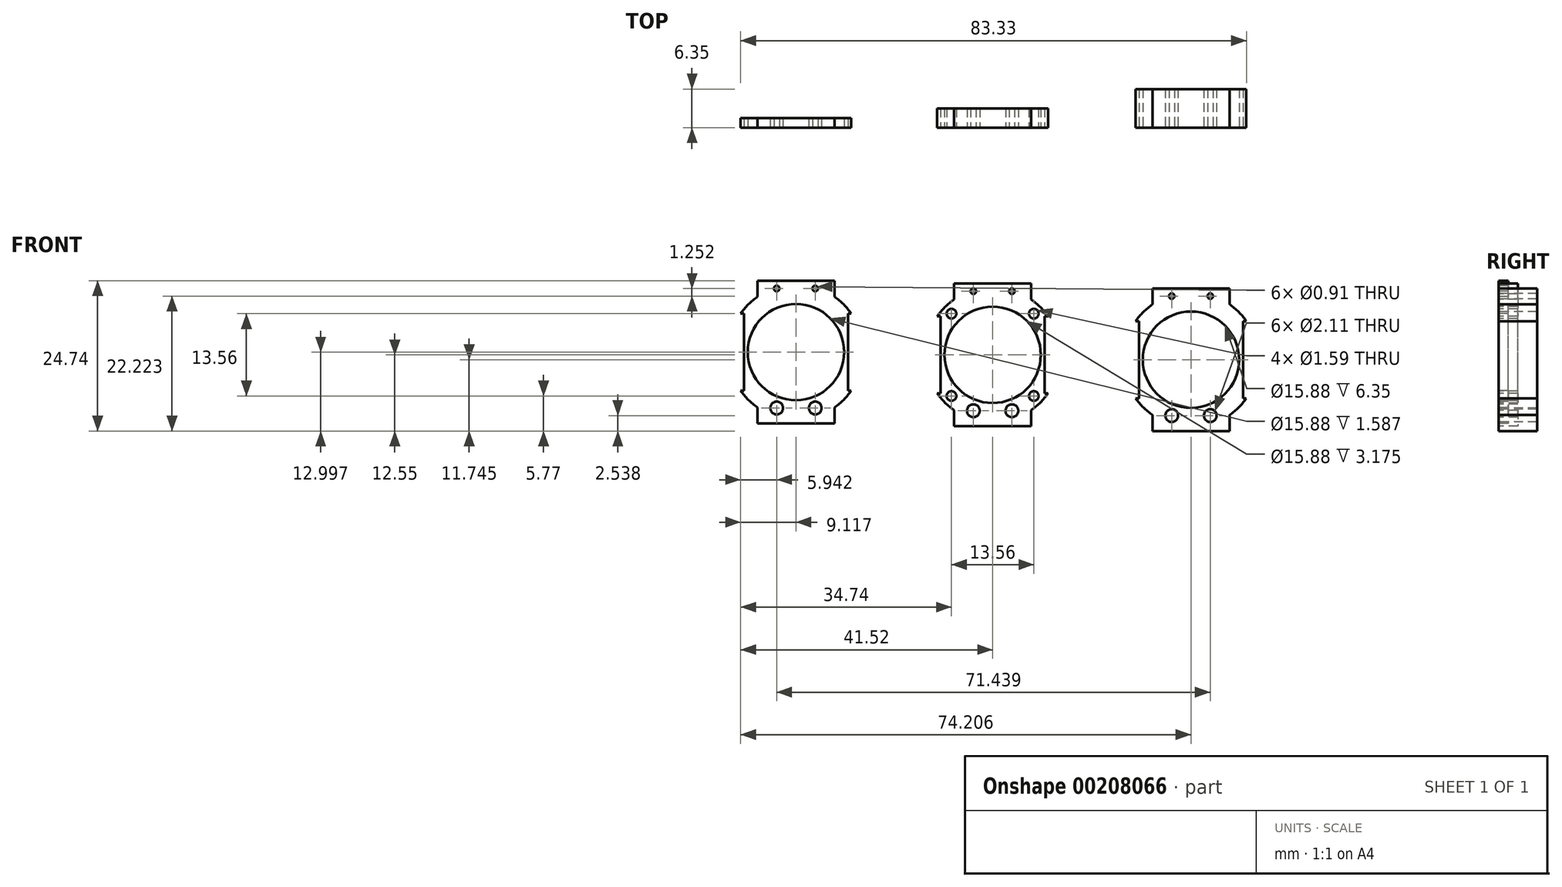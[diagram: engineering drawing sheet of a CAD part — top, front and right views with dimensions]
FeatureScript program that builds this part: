
annotation { "Feature Type Name" : "Feature", "Feature Type Description" : "" }
export const myFeature = defineFeature(function(context is Context, id is Id, definition is map)
    precondition{}
    {
        {
            var Q0;
            Q0=qCreatedBy(makeId("Front.planeOp"),FACE);
            var sketch = newSketch(context, id + "F0", { "sketchPlane" : qUnion([Q0])});
            skCircle(sketch, "E0", {"center": v(0, 0) * mm, "radius": 7.94 * mm});
            skCircle(sketch, "E1", {"center": v(0, 0) * mm, "radius": 11.11 * mm});
            skLineSegment(sketch, "E2", {"start": v(0, 15.5) * mm, "end": v(0, -17.4) * mm, "construction": true});
            skLineSegment(sketch, "E3", {"start": v(-15.84, 0) * mm, "end": v(17.27, 0) * mm, "construction": true});
            skLineSegment(sketch, "E4", {"start": v(-6.35, 12.66) * mm, "end": v(-6.35, -14.56) * mm, "construction": true});
            skLineSegment(sketch, "E5", {"start": v(6.35, -14.56) * mm, "end": v(6.35, 13.39) * mm, "construction": true});
            skLineSegment(sketch, "E6", {"start": v(-14.72, 6.35) * mm, "end": v(13.83, 6.35) * mm, "construction": true});
            skLineSegment(sketch, "E7", {"start": v(13.83, -6.35) * mm, "end": v(-15.12, -6.35) * mm, "construction": true});
            skLineSegment(sketch, "E8", {"start": v(0, 7.94) * mm, "end": v(-8.8, 7.94) * mm, "construction": true});
            skLineSegment(sketch, "E9", {"start": v(-7.94, 0) * mm, "end": v(-7.94, -9.09) * mm, "construction": true});
            skLineSegment(sketch, "E10", {"start": v(0, -7.94) * mm, "end": v(9.16, -7.94) * mm, "construction": true});
            skLineSegment(sketch, "E11", {"start": v(7.94, 0) * mm, "end": v(7.94, 8.95) * mm, "construction": true});
            skLineSegment(sketch, "E12", {"start": v(-6.35, 8.57) * mm, "end": v(6.35, 8.57) * mm});
            skLineSegment(sketch, "E13", {"start": v(6.35, 8.57) * mm, "end": v(6.35, 11.75) * mm});
            skLineSegment(sketch, "E14", {"start": v(6.35, 11.75) * mm, "end": v(-6.35, 11.75) * mm});
            skLineSegment(sketch, "E15", {"start": v(-6.35, 11.75) * mm, "end": v(-6.35, 8.57) * mm});
            skLineSegment(sketch, "E16", {"start": v(-8.57, -6.35) * mm, "end": v(-8.57, 6.35) * mm});
            skLineSegment(sketch, "E17", {"start": v(-8.57, 6.35) * mm, "end": v(-11.75, 6.35) * mm});
            skLineSegment(sketch, "E18", {"start": v(-11.75, 6.35) * mm, "end": v(-11.75, -6.35) * mm});
            skLineSegment(sketch, "E19", {"start": v(-11.75, -6.35) * mm, "end": v(-8.57, -6.35) * mm});
            skLineSegment(sketch, "E20", {"start": v(6.35, -8.57) * mm, "end": v(-6.35, -8.57) * mm});
            skLineSegment(sketch, "E21", {"start": v(-6.35, -8.57) * mm, "end": v(-6.35, -11.75) * mm});
            skLineSegment(sketch, "E22", {"start": v(-6.35, -11.75) * mm, "end": v(6.35, -11.75) * mm});
            skLineSegment(sketch, "E23", {"start": v(6.35, -11.75) * mm, "end": v(6.35, -8.57) * mm});
            skLineSegment(sketch, "E24", {"start": v(8.57, 6.35) * mm, "end": v(8.57, -6.35) * mm});
            skLineSegment(sketch, "E25", {"start": v(8.57, -6.35) * mm, "end": v(11.75, -6.35) * mm});
            skLineSegment(sketch, "E26", {"start": v(11.75, -6.35) * mm, "end": v(11.75, 6.35) * mm});
            skLineSegment(sketch, "E27", {"start": v(11.75, 6.35) * mm, "end": v(8.57, 6.35) * mm});
            skLineSegment(sketch, "E28", {"start": v(-7.33, 10.48) * mm, "end": v(7.08, 10.48) * mm, "construction": true});
            skPoint(sketch, "E29.startSnap0", {"position": v(-6.35, -10.16) * mm});
            skPoint(sketch, "E29.endSnap0", {"position": v(6.35, -10.16) * mm});
            skLineSegment(sketch, "E30", {"start": v(-3.17, 13.26) * mm, "end": v(-3.17, -13.35) * mm, "construction": true});
            skLineSegment(sketch, "E31", {"start": v(-3.17, -13.35) * mm, "end": v(3.18, -13.35) * mm, "construction": true});
            skLineSegment(sketch, "E32", {"start": v(3.18, -13.35) * mm, "end": v(3.18, 13.23) * mm, "construction": true});
            skCircle(sketch, "E33", {"center": v(-3.17, 10.48) * mm, "radius": 0.46 * mm});
            skCircle(sketch, "E34", {"center": v(3.18, 10.48) * mm, "radius": 0.46 * mm});
            skCircle(sketch, "E35", {"center": v(-3.17, -9.2) * mm, "radius": 1.05 * mm});
            skCircle(sketch, "E36", {"center": v(3.18, -9.2) * mm, "radius": 1.05 * mm});
            skLineSegment(sketch, "E37", {"start": v(-5.15, -9.2) * mm, "end": v(5.25, -9.2) * mm, "construction": true});
            skLineSegment(sketch, "E38", {"start": v(1.46, -9.2) * mm, "end": v(5.23, -9.2) * mm, "construction": true});
            skLineSegment(sketch, "E39", {"start": v(7.94, 0) * mm, "end": v(11.11, 0) * mm, "construction": true});
            skCircle(sketch, "E40", {"center": v(0, 0) * mm, "radius": 9.59 * mm, "construction": true});
            skLineSegment(sketch, "E41", {"start": v(0, 0) * mm, "end": v(-14.65, 14.65) * mm, "construction": true});
            skLineSegment(sketch, "E42", {"start": v(0, 0) * mm, "end": v(14.9, -14.9) * mm, "construction": true});
            skLineSegment(sketch, "E43", {"start": v(0, 0) * mm, "end": v(-14.95, -14.95) * mm, "construction": true});
            skLineSegment(sketch, "E44", {"start": v(0, 0) * mm, "end": v(15.1, 15.1) * mm, "construction": true});
            skCircle(sketch, "E45", {"center": v(-6.78, 6.78) * mm, "radius": 0.8 * mm});
            skCircle(sketch, "E46", {"center": v(6.78, 6.78) * mm, "radius": 0.8 * mm});
            skCircle(sketch, "E47", {"center": v(6.78, -6.78) * mm, "radius": 0.8 * mm});
            skCircle(sketch, "E48", {"center": v(-6.78, -6.78) * mm, "radius": 0.8 * mm});
            skSolve(sketch);
        }
        {
            var Q0;
            {var subQ0=sQuery(id+"F0.wireOp",EDGE,"E14");Q0=makeQuery(id+"F0.imprint","IMPRINT",FACE,{"disambiguationData":[TD([[makeQuery(id+"F0.imprint","IMPRINT",EDGE,{"derivedFrom":subQ0}),1.0]])]});}
            var Q1;
            {var subQ0=sQuery(id+"F0.wireOp",EDGE,"E22");Q1=makeQuery(id+"F0.imprint","IMPRINT",FACE,{"disambiguationData":[TD([[makeQuery(id+"F0.imprint","IMPRINT",EDGE,{"derivedFrom":subQ0}),1.0]])]});}
            var Q2;
            {var subQ5=sQuery(id+"F0.wireOp",EDGE,"E12");Q2=makeQuery(id+"F0.imprint","IMPRINT",FACE,{"disambiguationData":[TD([[makeQuery(id+"F0.imprint","IMPRINT",EDGE,{"derivedFrom":subQ5}),1.0]])]});}
            var Q3;
            {var subQ0=sQuery(id+"F0.wireOp",EDGE,"E20");Q3=makeQuery(id+"F0.imprint","IMPRINT",FACE,{"disambiguationData":[TD([[makeQuery(id+"F0.imprint","IMPRINT",EDGE,{"derivedFrom":subQ0}),1.0]])]});}
            var Q4;
            Q4=makeQuery(id+"F0.imprint","IMPRINT",FACE,{"disambiguationData":[TD([[makeQuery(id+"F0.imprint","IMPRINT",EDGE,{"derivedFrom":sQuery(id+"F0.wireOp",EDGE,"E0")}),-1.0]])]});
            extrude(context, id + "F1", {"entities" : qUnion([Q0, Q1, Q2, Q3, Q4]), "oppositeDirection" : true, "depth" : 3.17 * mm});
        }
        {
            var Q0;
            Q0=qCreatedBy(makeId("Front.planeOp"),FACE);
            var sketch = newSketch(context, id + "F2", { "sketchPlane" : qUnion([Q0])});
            skCircle(sketch, "E49", {"center": v(-58, 54.06) * mm, "radius": 7.94 * mm});
            skCircle(sketch, "E50", {"center": v(-58, 54.06) * mm, "radius": 11.11 * mm});
            skLineSegment(sketch, "E51", {"start": v(-58, 71.11) * mm, "end": v(-58, 38.2) * mm, "construction": true});
            skLineSegment(sketch, "E52", {"start": v(-73.79, 54.06) * mm, "end": v(-40.67, 54.06) * mm, "construction": true});
            skLineSegment(sketch, "E53", {"start": v(-64.34, 68.27) * mm, "end": v(-64.34, 41.05) * mm, "construction": true});
            skLineSegment(sketch, "E54", {"start": v(-51.64, 41.05) * mm, "end": v(-51.64, 69) * mm, "construction": true});
            skLineSegment(sketch, "E55", {"start": v(-72.66, 60.4) * mm, "end": v(-44.12, 60.4) * mm, "construction": true});
            skLineSegment(sketch, "E56", {"start": v(-44.12, 47.7) * mm, "end": v(-73.06, 47.7) * mm, "construction": true});
            skLineSegment(sketch, "E57", {"start": v(-58, 62) * mm, "end": v(-66.74, 62) * mm, "construction": true});
            skLineSegment(sketch, "E58", {"start": v(-65.93, 54.06) * mm, "end": v(-65.93, 46.53) * mm, "construction": true});
            skLineSegment(sketch, "E59", {"start": v(-58, 46.12) * mm, "end": v(-48.79, 46.12) * mm, "construction": true});
            skLineSegment(sketch, "E60", {"start": v(-50.05, 54.06) * mm, "end": v(-50.05, 64.57) * mm, "construction": true});
            skLineSegment(sketch, "E61", {"start": v(-64.34, 62.63) * mm, "end": v(-51.64, 62.63) * mm});
            skLineSegment(sketch, "E62", {"start": v(-51.64, 62.63) * mm, "end": v(-51.64, 65.8) * mm});
            skLineSegment(sketch, "E63", {"start": v(-51.64, 65.8) * mm, "end": v(-64.34, 65.8) * mm});
            skLineSegment(sketch, "E64", {"start": v(-64.34, 65.8) * mm, "end": v(-64.34, 62.63) * mm});
            skLineSegment(sketch, "E65", {"start": v(-66.56, 47.7) * mm, "end": v(-66.56, 60.4) * mm});
            skLineSegment(sketch, "E66", {"start": v(-66.56, 60.4) * mm, "end": v(-69.74, 60.4) * mm});
            skLineSegment(sketch, "E67", {"start": v(-69.74, 60.4) * mm, "end": v(-69.74, 47.7) * mm});
            skLineSegment(sketch, "E68", {"start": v(-69.74, 47.7) * mm, "end": v(-66.56, 47.7) * mm});
            skLineSegment(sketch, "E69", {"start": v(-51.64, 45.49) * mm, "end": v(-64.34, 45.49) * mm});
            skLineSegment(sketch, "E70", {"start": v(-64.34, 45.49) * mm, "end": v(-64.34, 42.31) * mm});
            skLineSegment(sketch, "E71", {"start": v(-64.34, 42.31) * mm, "end": v(-51.64, 42.31) * mm});
            skLineSegment(sketch, "E72", {"start": v(-51.64, 42.31) * mm, "end": v(-51.64, 45.49) * mm});
            skLineSegment(sketch, "E73", {"start": v(-49.42, 60.4) * mm, "end": v(-49.42, 47.7) * mm});
            skLineSegment(sketch, "E74", {"start": v(-49.42, 47.7) * mm, "end": v(-46.24, 47.7) * mm});
            skLineSegment(sketch, "E75", {"start": v(-46.24, 47.7) * mm, "end": v(-46.24, 60.4) * mm});
            skLineSegment(sketch, "E76", {"start": v(-46.24, 60.4) * mm, "end": v(-49.42, 60.4) * mm});
            skLineSegment(sketch, "E77", {"start": v(-65.27, 64.54) * mm, "end": v(-50.86, 64.54) * mm, "construction": true});
            skPoint(sketch, "E78.startSnap0", {"position": v(-64.34, 43.9) * mm});
            skPoint(sketch, "E78.endSnap0", {"position": v(-51.64, 43.9) * mm});
            skLineSegment(sketch, "E79", {"start": v(-61.17, 68.88) * mm, "end": v(-61.17, 40.7) * mm, "construction": true});
            skLineSegment(sketch, "E80", {"start": v(-61.17, 40.7) * mm, "end": v(-54.82, 40.7) * mm, "construction": true});
            skLineSegment(sketch, "E81", {"start": v(-54.82, 40.7) * mm, "end": v(-54.82, 68.84) * mm, "construction": true});
            skCircle(sketch, "E82", {"center": v(-61.17, 64.54) * mm, "radius": 0.46 * mm});
            skCircle(sketch, "E83", {"center": v(-54.82, 64.54) * mm, "radius": 0.46 * mm});
            skCircle(sketch, "E84", {"center": v(-61.17, 44.85) * mm, "radius": 1.05 * mm});
            skCircle(sketch, "E85", {"center": v(-54.82, 44.85) * mm, "radius": 1.05 * mm});
            skLineSegment(sketch, "E86", {"start": v(-63.1, 44.85) * mm, "end": v(-52.69, 44.85) * mm, "construction": true});
            skLineSegment(sketch, "E87", {"start": v(-56.48, 44.85) * mm, "end": v(-52.72, 44.85) * mm, "construction": true});
            skSolve(sketch);
        }
        {
            var Q0;
            Q0=makeQuery(id+"F2.imprint","IMPRINT",FACE,{"disambiguationData":[TD([[makeQuery(id+"F2.imprint","IMPRINT",EDGE,{"derivedFrom":sQuery(id+"F2.wireOp",EDGE,"E49")}),-1.0]])]});
            var Q1;
            {var subQ0=sQuery(id+"F2.wireOp",EDGE,"E63");Q1=makeQuery(id+"F2.imprint","IMPRINT",FACE,{"disambiguationData":[TD([[makeQuery(id+"F2.imprint","IMPRINT",EDGE,{"derivedFrom":subQ0}),1.0]])]});}
            var Q2;
            {var subQ0=sQuery(id+"F2.wireOp",EDGE,"E61");Q2=makeQuery(id+"F2.imprint","IMPRINT",FACE,{"disambiguationData":[TD([[makeQuery(id+"F2.imprint","IMPRINT",EDGE,{"derivedFrom":subQ0}),1.0]])]});}
            var Q3;
            {var subQ0=sQuery(id+"F2.wireOp",EDGE,"E69");Q3=makeQuery(id+"F2.imprint","IMPRINT",FACE,{"disambiguationData":[TD([[makeQuery(id+"F2.imprint","IMPRINT",EDGE,{"derivedFrom":subQ0}),1.0]])]});}
            var Q4;
            {var subQ0=sQuery(id+"F2.wireOp",EDGE,"E71");Q4=makeQuery(id+"F2.imprint","IMPRINT",FACE,{"disambiguationData":[TD([[makeQuery(id+"F2.imprint","IMPRINT",EDGE,{"derivedFrom":subQ0}),1.0]])]});}
            extrude(context, id + "F3", {"entities" : qUnion([Q0, Q1, Q2, Q3, Q4]), "oppositeDirection" : true, "depth" : 6.35 * mm});
        }
        {
            var Q0;
            Q0=makeQuery(id+"F3.opExtrude","SWEPT_BODY",BODY,{"disambiguationData":[OSD([sQuery(id+"F2.wireOp",EDGE,"E49"),sQuery(id+"F2.wireOp",EDGE,"E50"),sQuery(id+"F2.wireOp",EDGE,"E62"),sQuery(id+"F2.wireOp",EDGE,"E63"),sQuery(id+"F2.wireOp",EDGE,"E64"),sQuery(id+"F2.wireOp",EDGE,"E65"),sQuery(id+"F2.wireOp",EDGE,"E66"),sQuery(id+"F2.wireOp",EDGE,"E68"),sQuery(id+"F2.wireOp",EDGE,"E70"),sQuery(id+"F2.wireOp",EDGE,"E71"),sQuery(id+"F2.wireOp",EDGE,"E72"),sQuery(id+"F2.wireOp",EDGE,"E73"),sQuery(id+"F2.wireOp",EDGE,"E74"),sQuery(id+"F2.wireOp",EDGE,"E76"),sQuery(id+"F2.wireOp",EDGE,"E82"),sQuery(id+"F2.wireOp",EDGE,"E83"),sQuery(id+"F2.wireOp",EDGE,"E84"),sQuery(id+"F2.wireOp",EDGE,"E85")])]});
            transform(context, id + "F4", {"entities" : qUnion([Q0]), "transformType" : TransformType.TRANSLATION_3D, "dx" : 90.68 * mm, "dy" : 0 * mm, "dz" : -52.58 * mm, "makeCopy" : false});
        }
        {
            var Q0;
            Q0=qCreatedBy(makeId("Front.planeOp"),FACE);
            var sketch = newSketch(context, id + "F5", { "sketchPlane" : qUnion([Q0])});
            skCircle(sketch, "E88", {"center": v(-101.24, 6.54) * mm, "radius": 7.94 * mm});
            skCircle(sketch, "E89", {"center": v(-101.24, 6.54) * mm, "radius": 11.11 * mm});
            skLineSegment(sketch, "E90", {"start": v(-101.24, 22.04) * mm, "end": v(-101.24, -10.87) * mm, "construction": true});
            skLineSegment(sketch, "E91", {"start": v(-117.08, 6.54) * mm, "end": v(-83.97, 6.54) * mm, "construction": true});
            skLineSegment(sketch, "E92", {"start": v(-107.59, 19.2) * mm, "end": v(-107.59, -8.02) * mm, "construction": true});
            skLineSegment(sketch, "E93", {"start": v(-94.89, -8.02) * mm, "end": v(-94.89, 19.93) * mm, "construction": true});
            skLineSegment(sketch, "E94", {"start": v(-115.96, 12.9) * mm, "end": v(-87.41, 12.9) * mm, "construction": true});
            skLineSegment(sketch, "E95", {"start": v(-87.41, 0.2) * mm, "end": v(-116.35, 0.2) * mm, "construction": true});
            skLineSegment(sketch, "E96", {"start": v(-101.24, 14.48) * mm, "end": v(-110.04, 14.48) * mm, "construction": true});
            skLineSegment(sketch, "E97", {"start": v(-109.17, 6.54) * mm, "end": v(-109.17, -2.54) * mm, "construction": true});
            skLineSegment(sketch, "E98", {"start": v(-101.24, -1.4) * mm, "end": v(-92.08, -1.4) * mm, "construction": true});
            skLineSegment(sketch, "E99", {"start": v(-93.3, 6.54) * mm, "end": v(-93.3, 15.5) * mm, "construction": true});
            skLineSegment(sketch, "E100", {"start": v(-107.59, 15.12) * mm, "end": v(-94.89, 15.12) * mm});
            skLineSegment(sketch, "E101", {"start": v(-94.89, 15.12) * mm, "end": v(-94.89, 18.3) * mm});
            skLineSegment(sketch, "E102", {"start": v(-94.89, 18.3) * mm, "end": v(-107.59, 18.3) * mm});
            skLineSegment(sketch, "E103", {"start": v(-107.59, 18.3) * mm, "end": v(-107.59, 15.12) * mm});
            skLineSegment(sketch, "E104", {"start": v(-109.8, 0.2) * mm, "end": v(-109.8, 12.9) * mm});
            skLineSegment(sketch, "E105", {"start": v(-109.8, 12.9) * mm, "end": v(-112.98, 12.9) * mm});
            skLineSegment(sketch, "E106", {"start": v(-112.98, 12.9) * mm, "end": v(-112.98, 0.2) * mm});
            skLineSegment(sketch, "E107", {"start": v(-112.98, 0.2) * mm, "end": v(-109.8, 0.2) * mm});
            skLineSegment(sketch, "E108", {"start": v(-94.89, -2.03) * mm, "end": v(-107.59, -2.03) * mm});
            skLineSegment(sketch, "E109", {"start": v(-107.59, -2.03) * mm, "end": v(-107.59, -5.2) * mm});
            skLineSegment(sketch, "E110", {"start": v(-107.59, -5.2) * mm, "end": v(-94.89, -5.2) * mm});
            skLineSegment(sketch, "E111", {"start": v(-94.89, -5.2) * mm, "end": v(-94.89, -2.03) * mm});
            skLineSegment(sketch, "E112", {"start": v(-92.66, 12.9) * mm, "end": v(-92.66, 0.2) * mm});
            skLineSegment(sketch, "E113", {"start": v(-92.66, 0.2) * mm, "end": v(-89.49, 0.2) * mm});
            skLineSegment(sketch, "E114", {"start": v(-89.49, 0.2) * mm, "end": v(-89.49, 12.9) * mm});
            skLineSegment(sketch, "E115", {"start": v(-89.49, 12.9) * mm, "end": v(-92.66, 12.9) * mm});
            skLineSegment(sketch, "E116", {"start": v(-108.57, 17.02) * mm, "end": v(-94.15, 17.02) * mm, "construction": true});
            skPoint(sketch, "E117.startSnap0", {"position": v(-107.59, -3.62) * mm});
            skPoint(sketch, "E117.endSnap0", {"position": v(-94.89, -3.62) * mm});
            skLineSegment(sketch, "E118", {"start": v(-104.41, 19.8) * mm, "end": v(-104.41, -6.81) * mm, "construction": true});
            skLineSegment(sketch, "E119", {"start": v(-104.41, -6.81) * mm, "end": v(-98.06, -6.81) * mm, "construction": true});
            skLineSegment(sketch, "E120", {"start": v(-98.06, -6.81) * mm, "end": v(-98.06, 19.77) * mm, "construction": true});
            skCircle(sketch, "E121", {"center": v(-104.41, 17.02) * mm, "radius": 0.46 * mm});
            skCircle(sketch, "E122", {"center": v(-98.06, 17.02) * mm, "radius": 0.46 * mm});
            skCircle(sketch, "E123", {"center": v(-104.41, -2.66) * mm, "radius": 1.05 * mm});
            skCircle(sketch, "E124", {"center": v(-98.06, -2.66) * mm, "radius": 1.05 * mm});
            skLineSegment(sketch, "E125", {"start": v(-106.39, -2.66) * mm, "end": v(-95.99, -2.66) * mm, "construction": true});
            skLineSegment(sketch, "E126", {"start": v(-99.77, -2.66) * mm, "end": v(-96.01, -2.66) * mm, "construction": true});
            skSolve(sketch);
        }
        {
            var Q0;
            Q0=makeQuery(id+"F5.imprint","IMPRINT",FACE,{"disambiguationData":[TD([[makeQuery(id+"F5.imprint","IMPRINT",EDGE,{"derivedFrom":sQuery(id+"F5.wireOp",EDGE,"E88")}),-1.0]])]});
            var Q1;
            {var subQ0=sQuery(id+"F5.wireOp",EDGE,"E100");Q1=makeQuery(id+"F5.imprint","IMPRINT",FACE,{"disambiguationData":[TD([[makeQuery(id+"F5.imprint","IMPRINT",EDGE,{"derivedFrom":subQ0}),1.0]])]});}
            var Q2;
            {var subQ0=sQuery(id+"F5.wireOp",EDGE,"E102");Q2=makeQuery(id+"F5.imprint","IMPRINT",FACE,{"disambiguationData":[TD([[makeQuery(id+"F5.imprint","IMPRINT",EDGE,{"derivedFrom":subQ0}),1.0]])]});}
            var Q3;
            {var subQ0=sQuery(id+"F5.wireOp",EDGE,"E108");Q3=makeQuery(id+"F5.imprint","IMPRINT",FACE,{"disambiguationData":[TD([[makeQuery(id+"F5.imprint","IMPRINT",EDGE,{"derivedFrom":subQ0}),1.0]])]});}
            var Q4;
            {var subQ0=sQuery(id+"F5.wireOp",EDGE,"E110");Q4=makeQuery(id+"F5.imprint","IMPRINT",FACE,{"disambiguationData":[TD([[makeQuery(id+"F5.imprint","IMPRINT",EDGE,{"derivedFrom":subQ0}),1.0]])]});}
            extrude(context, id + "F6", {"entities" : qUnion([Q0, Q1, Q2, Q3, Q4]), "oppositeDirection" : true, "depth" : 1.59 * mm});
        }
        {
            var Q0;
            Q0=makeQuery(id+"F6.opExtrude","SWEPT_BODY",BODY,{"disambiguationData":[OSD([sQuery(id+"F5.wireOp",EDGE,"E88"),sQuery(id+"F5.wireOp",EDGE,"E89"),sQuery(id+"F5.wireOp",EDGE,"E101"),sQuery(id+"F5.wireOp",EDGE,"E102"),sQuery(id+"F5.wireOp",EDGE,"E103"),sQuery(id+"F5.wireOp",EDGE,"E104"),sQuery(id+"F5.wireOp",EDGE,"E105"),sQuery(id+"F5.wireOp",EDGE,"E107"),sQuery(id+"F5.wireOp",EDGE,"E109"),sQuery(id+"F5.wireOp",EDGE,"E110"),sQuery(id+"F5.wireOp",EDGE,"E111"),sQuery(id+"F5.wireOp",EDGE,"E112"),sQuery(id+"F5.wireOp",EDGE,"E113"),sQuery(id+"F5.wireOp",EDGE,"E115"),sQuery(id+"F5.wireOp",EDGE,"E121"),sQuery(id+"F5.wireOp",EDGE,"E122"),sQuery(id+"F5.wireOp",EDGE,"E123"),sQuery(id+"F5.wireOp",EDGE,"E124")])]});
            transform(context, id + "F7", {"entities" : qUnion([Q0]), "transformType" : TransformType.TRANSLATION_3D, "dx" : 68.83 * mm, "dy" : 0 * mm, "dz" : 0 * mm, "makeCopy" : false});
        }
        {
            var Q0;
            Q0=makeQuery(id+"F6.opExtrude","SWEPT_BODY",BODY,{"disambiguationData":[OSD([sQuery(id+"F5.wireOp",EDGE,"E88"),sQuery(id+"F5.wireOp",EDGE,"E89"),sQuery(id+"F5.wireOp",EDGE,"E101"),sQuery(id+"F5.wireOp",EDGE,"E102"),sQuery(id+"F5.wireOp",EDGE,"E103"),sQuery(id+"F5.wireOp",EDGE,"E104"),sQuery(id+"F5.wireOp",EDGE,"E105"),sQuery(id+"F5.wireOp",EDGE,"E107"),sQuery(id+"F5.wireOp",EDGE,"E109"),sQuery(id+"F5.wireOp",EDGE,"E110"),sQuery(id+"F5.wireOp",EDGE,"E111"),sQuery(id+"F5.wireOp",EDGE,"E112"),sQuery(id+"F5.wireOp",EDGE,"E113"),sQuery(id+"F5.wireOp",EDGE,"E115"),sQuery(id+"F5.wireOp",EDGE,"E121"),sQuery(id+"F5.wireOp",EDGE,"E122"),sQuery(id+"F5.wireOp",EDGE,"E123"),sQuery(id+"F5.wireOp",EDGE,"E124")])]});
            transform(context, id + "F8", {"entities" : qUnion([Q0]), "transformType" : TransformType.TRANSLATION_3D, "dx" : 0 * mm, "dy" : 0 * mm, "dz" : -6.1 * mm, "makeCopy" : false});
        }
        {
            var Q0;
            Q0=makeQuery(id+"F3.opExtrude","SWEPT_BODY",BODY,{"disambiguationData":[OSD([sQuery(id+"F2.wireOp",EDGE,"E49"),sQuery(id+"F2.wireOp",EDGE,"E50"),sQuery(id+"F2.wireOp",EDGE,"E62"),sQuery(id+"F2.wireOp",EDGE,"E63"),sQuery(id+"F2.wireOp",EDGE,"E64"),sQuery(id+"F2.wireOp",EDGE,"E65"),sQuery(id+"F2.wireOp",EDGE,"E66"),sQuery(id+"F2.wireOp",EDGE,"E68"),sQuery(id+"F2.wireOp",EDGE,"E70"),sQuery(id+"F2.wireOp",EDGE,"E71"),sQuery(id+"F2.wireOp",EDGE,"E72"),sQuery(id+"F2.wireOp",EDGE,"E73"),sQuery(id+"F2.wireOp",EDGE,"E74"),sQuery(id+"F2.wireOp",EDGE,"E76"),sQuery(id+"F2.wireOp",EDGE,"E82"),sQuery(id+"F2.wireOp",EDGE,"E83"),sQuery(id+"F2.wireOp",EDGE,"E84"),sQuery(id+"F2.wireOp",EDGE,"E85")])]});
            transform(context, id + "F9", {"entities" : qUnion([Q0]), "transformType" : TransformType.TRANSLATION_3D, "dx" : 0 * mm, "dy" : 0 * mm, "dz" : -2.3 * mm, "makeCopy" : false});
        }
    });
